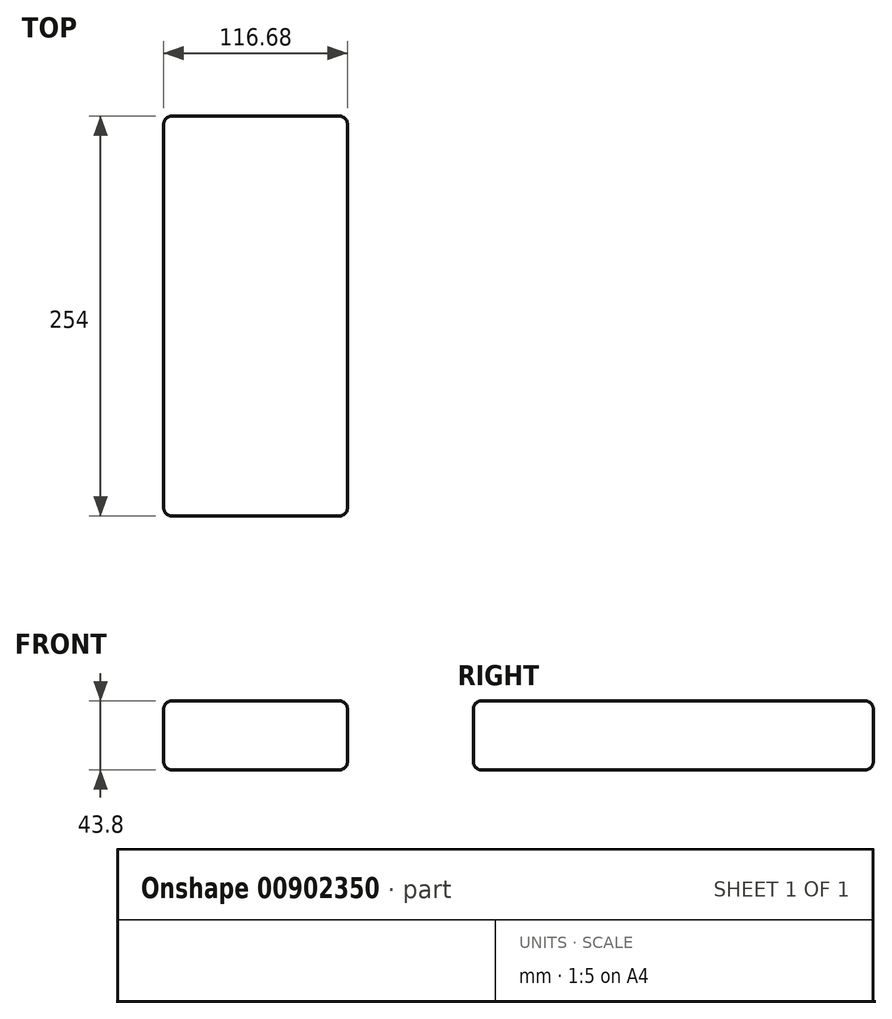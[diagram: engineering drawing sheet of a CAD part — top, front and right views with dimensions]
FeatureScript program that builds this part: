
annotation { "Feature Type Name" : "Feature", "Feature Type Description" : "" }
export const myFeature = defineFeature(function(context is Context, id is Id, definition is map)
    precondition{}
    {
        {
            var Q0;
            Q0=qCreatedBy(makeId("Front.planeOp"),FACE);
            var sketch = newSketch(context, id + "F0", { "sketchPlane" : qUnion([Q0])});
            skLineSegment(sketch, "E0.bottom", {"start": v(58.34, -21.9) * mm, "end": v(-58.34, -21.9) * mm});
            skLineSegment(sketch, "E0.top", {"start": v(58.34, 21.9) * mm, "end": v(-58.34, 21.9) * mm});
            skLineSegment(sketch, "E0.left", {"start": v(58.34, -21.9) * mm, "end": v(58.34, 21.9) * mm});
            skLineSegment(sketch, "E0.right", {"start": v(-58.34, -21.9) * mm, "end": v(-58.34, 21.9) * mm});
            skPoint(sketch, "E0.middle", {"position": v(0, 0) * mm});
            skSolve(sketch);
        }
        {
            var Q0;
            Q0=makeQuery(id+"F0.imprint","IMPRINT",FACE,{"disambiguationData":[TD([[makeQuery(id+"F0.imprint","IMPRINT",EDGE,{"derivedFrom":sQuery(id+"F0.wireOp",EDGE,"E0.bottom")}),-1.0]])]});
            extrude(context, id + "F1", {"entities" : qUnion([Q0]), "oppositeDirection" : true, "depth" : 254 * mm, "offsetDistance" : 25.4 * mm});
        }
        {
            var Q0;
            Q0=makeQuery(id+"F1.opExtrude","SWEPT_FACE",FACE,{"disambiguationData":[OSD([sQuery(id+"F0.wireOp",EDGE,"E0.right")])]});
            var Q1;
            Q1=makeQuery(id+"F1.opExtrude","CAP_FACE",FACE,{"disambiguationData":[OSD([sQuery(id+"F0.wireOp",EDGE,"E0.bottom"),sQuery(id+"F0.wireOp",EDGE,"E0.top"),sQuery(id+"F0.wireOp",EDGE,"E0.left"),sQuery(id+"F0.wireOp",EDGE,"E0.right")])],"isStart":true});
            var Q2;
            Q2=makeQuery(id+"F1.opExtrude","SWEPT_FACE",FACE,{"disambiguationData":[OSD([sQuery(id+"F0.wireOp",EDGE,"E0.left")])]});
            var Q3;
            Q3=makeQuery(id+"F1.opExtrude","CAP_FACE",FACE,{"disambiguationData":[OSD([sQuery(id+"F0.wireOp",EDGE,"E0.bottom"),sQuery(id+"F0.wireOp",EDGE,"E0.top"),sQuery(id+"F0.wireOp",EDGE,"E0.left"),sQuery(id+"F0.wireOp",EDGE,"E0.right")])],"isStart":false});
            fillet(context, id + "F2", {"entities" : qUnion([Q0, Q1, Q2, Q3]), "radius" : 5.08 * mm, "tangentPropagation" : true, "allowEdgeOverflow" : false});
        }
    });
